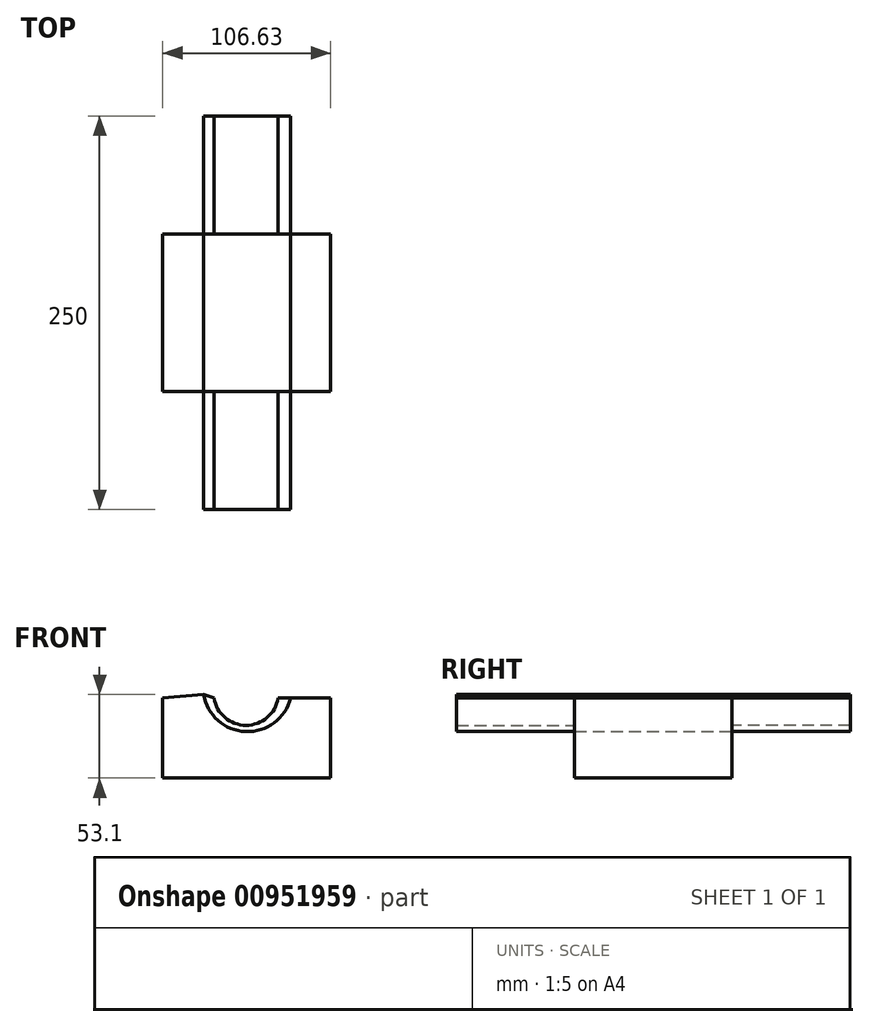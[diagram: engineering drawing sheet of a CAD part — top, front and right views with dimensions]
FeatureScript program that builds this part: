
annotation { "Feature Type Name" : "Feature", "Feature Type Description" : "" }
export const myFeature = defineFeature(function(context is Context, id is Id, definition is map)
    precondition{}
    {
        {
            var Q0;
            Q0=qCreatedBy(makeId("Front.planeOp"),FACE);
            var sketch = newSketch(context, id + "F0", { "sketchPlane" : qUnion([Q0])});
            skArc(sketch, "E0", {"start": v(-19.53, 14.26) * mm, "mid": v(0.95, 0.37) * mm, "end": v(21.72, 13.82) * mm});
            skArc(sketch, "E1", {"start": v(-26.1, 16.02) * mm, "mid": v(0.64, -7.58) * mm, "end": v(29.18, 13.82) * mm});
            skLineSegment(sketch, "E2", {"start": v(-26.1, 16.02) * mm, "end": v(-19.53, 14.26) * mm});
            skLineSegment(sketch, "E3", {"start": v(21.72, 13.82) * mm, "end": v(29.18, 13.82) * mm});
            skLineSegment(sketch, "E4", {"start": v(29.18, 13.82) * mm, "end": v(54.63, 13.82) * mm});
            skLineSegment(sketch, "E5", {"start": v(54.63, 13.82) * mm, "end": v(54.63, -37.08) * mm});
            skLineSegment(sketch, "E6", {"start": v(54.63, -37.08) * mm, "end": v(-52, -37.08) * mm});
            skLineSegment(sketch, "E7", {"start": v(-52, -37.08) * mm, "end": v(-52, 13.82) * mm});
            skLineSegment(sketch, "E8", {"start": v(-52, 13.82) * mm, "end": v(-26.1, 16.02) * mm});
            skSolve(sketch);
        }
        {
            var Q0;
            Q0=makeQuery(id+"F0.imprint","IMPRINT",FACE,{"disambiguationData":[TD([[makeQuery(id+"F0.imprint","IMPRINT",EDGE,{"derivedFrom":sQuery(id+"F0.wireOp",EDGE,"E1")}),-1.0]])]});
            extrude(context, id + "F1", {"entities" : qUnion([Q0]), "depth" : 50 * mm, "offsetDistance" : 25 * mm});
        }
        {
            var Q0;
            Q0=makeQuery(id+"F1.opExtrude","CAP_FACE",FACE,{"disambiguationData":[OSD([sQuery(id+"F0.wireOp",EDGE,"E1"),sQuery(id+"F0.wireOp",EDGE,"E4"),sQuery(id+"F0.wireOp",EDGE,"E5"),sQuery(id+"F0.wireOp",EDGE,"E6"),sQuery(id+"F0.wireOp",EDGE,"E7"),sQuery(id+"F0.wireOp",EDGE,"E8")])],"isStart":false});
            var sketch = newSketch(context, id + "F2", { "sketchPlane" : qUnion([Q0])});
            skArc(sketch, "E9", {"start": v(-26.1, 16.02) * mm, "mid": v(0.63, -8.02) * mm, "end": v(29.18, 13.82) * mm});
            skArc(sketch, "E10", {"start": v(-19.53, 13.82) * mm, "mid": v(0.88, -3.6) * mm, "end": v(21.28, 13.82) * mm});
            skLineSegment(sketch, "E11", {"start": v(-26.1, 16.02) * mm, "end": v(-19.53, 13.82) * mm});
            skLineSegment(sketch, "E12", {"start": v(21.28, 13.82) * mm, "end": v(29.18, 13.82) * mm});
            skSolve(sketch);
        }
        {
            var Q0;
            Q0=makeQuery(id+"F2.imprint","IMPRINT",FACE,{"disambiguationData":[TD([[makeQuery(id+"F2.imprint","IMPRINT",EDGE,{"derivedFrom":sQuery(id+"F2.wireOp",EDGE,"E10")}),-1.0]])]});
            extrude(context, id + "F3", {"entities" : qUnion([Q0]), "depth" : 75 * mm, "offsetDistance" : 25 * mm});
        }
        {
            var Q0;
            Q0=makeQuery(id+"F3.opExtrude","SWEPT_BODY",BODY,{"disambiguationData":[OSD([sQuery(id+"F0.wireOp",EDGE,"E1"),sQuery(id+"F2.wireOp",EDGE,"E10"),sQuery(id+"F2.wireOp",EDGE,"E11"),sQuery(id+"F2.wireOp",EDGE,"E12")])]});
            var Q1;
            Q1=makeQuery(id+"F1.opExtrude","SWEPT_BODY",BODY,{"disambiguationData":[OSD([sQuery(id+"F0.wireOp",EDGE,"E1"),sQuery(id+"F0.wireOp",EDGE,"E4"),sQuery(id+"F0.wireOp",EDGE,"E5"),sQuery(id+"F0.wireOp",EDGE,"E6"),sQuery(id+"F0.wireOp",EDGE,"E7"),sQuery(id+"F0.wireOp",EDGE,"E8")])]});
            var Q2;
            Q2=makeQuery(id+"F1.opExtrude","CAP_FACE",FACE,{"disambiguationData":[OSD([sQuery(id+"F0.wireOp",EDGE,"E1"),sQuery(id+"F0.wireOp",EDGE,"E4"),sQuery(id+"F0.wireOp",EDGE,"E5"),sQuery(id+"F0.wireOp",EDGE,"E6"),sQuery(id+"F0.wireOp",EDGE,"E7"),sQuery(id+"F0.wireOp",EDGE,"E8")])],"isStart":true});
            mirror(context, id + "F4", {"operationType" : NewBodyOperationType.ADD, "entities" : qUnion([Q0, Q1]), "mirrorPlane" : qUnion([Q2])});
        }
    });
